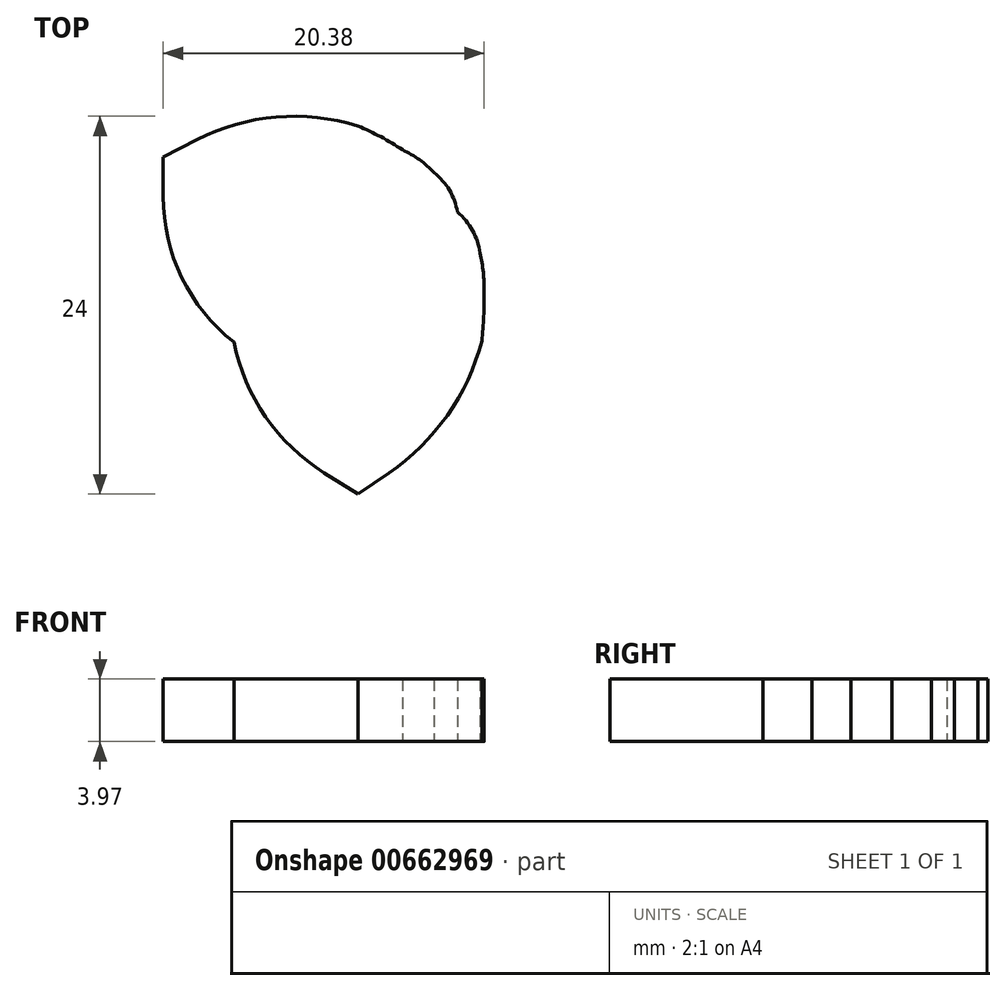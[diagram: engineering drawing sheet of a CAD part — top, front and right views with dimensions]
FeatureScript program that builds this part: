
annotation { "Feature Type Name" : "Feature", "Feature Type Description" : "" }
export const myFeature = defineFeature(function(context is Context, id is Id, definition is map)
    precondition{}
    {
        {
            var Q0;
            Q0=qCreatedBy(makeId("Top.planeOp"),FACE);
            var sketch = newSketch(context, id + "F0", { "sketchPlane" : qUnion([Q0])});
            skPoint(sketch, "E0.center", {"position": v(0, 0) * mm});
            skLineSegment(sketch, "E1", {"start": v(-10.2, 8.25) * mm, "end": v(-12.37, 7.15) * mm});
            skLineSegment(sketch, "E2", {"start": v(-12.37, 7.15) * mm, "end": v(-12.37, 4.64) * mm});
            skLineSegment(sketch, "E3", {"start": v(1.97, -12.9) * mm, "end": v(0, -14.26) * mm});
            skLineSegment(sketch, "E4", {"start": v(0, -14.26) * mm, "end": v(-2.14, -12.9) * mm});
            skLineSegment(sketch, "E5", {"start": v(-12.37, 4.64) * mm, "end": v(-12.37, 4.57) * mm});
            skArc(sketch, "E6", {"start": v(0, 9.12) * mm, "mid": v(-5.19, 9.69) * mm, "end": v(-10.2, 8.25) * mm});
            skArc(sketch, "E7", {"start": v(-7.87, -4.61) * mm, "mid": v(-5.86, -9.35) * mm, "end": v(-2.14, -12.9) * mm});
            skArc(sketch, "E8", {"start": v(-12.37, 4.64) * mm, "mid": v(-11.19, -0.5) * mm, "end": v(-7.87, -4.61) * mm});
            skArc(sketch, "E9", {"start": v(4.84, 6.15) * mm, "mid": v(3.9, 6.98) * mm, "end": v(2.84, 7.61) * mm});
            skArc(sketch, "E10", {"start": v(6.33, 3.65) * mm, "mid": v(5.82, 5.04) * mm, "end": v(4.84, 6.15) * mm});
            skArc(sketch, "E11.trimOffspring", {"start": v(2.84, 7.61) * mm, "mid": v(1.46, 8.44) * mm, "end": v(0, 9.12) * mm});
            skArc(sketch, "E12", {"start": v(1.97, -12.9) * mm, "mid": v(5.68, -9.25) * mm, "end": v(7.87, -4.53) * mm});
            skArc(sketch, "E13", {"start": v(7.87, -4.53) * mm, "mid": v(8, -2.98) * mm, "end": v(8, -1.42) * mm});
            skArc(sketch, "E14", {"start": v(8, -1.42) * mm, "mid": v(7.97, -0.18) * mm, "end": v(7.76, 1.05) * mm});
            skArc(sketch, "E15", {"start": v(7.76, 1.05) * mm, "mid": v(7.28, 2.48) * mm, "end": v(6.33, 3.65) * mm});
            skSolve(sketch);
        }
        {
            var Q0;
            Q0=makeQuery(id+"F0.imprint","IMPRINT",FACE,{"disambiguationData":[TD([[makeQuery(id+"F0.imprint","IMPRINT",EDGE,{"derivedFrom":sQuery(id+"F0.wireOp",EDGE,"E1")}),1.0]])]});
            extrude(context, id + "F1", {"entities" : qUnion([Q0]), "depth" : 3.97 * mm, "offsetDistance" : 25.4 * mm});
        }
    });
